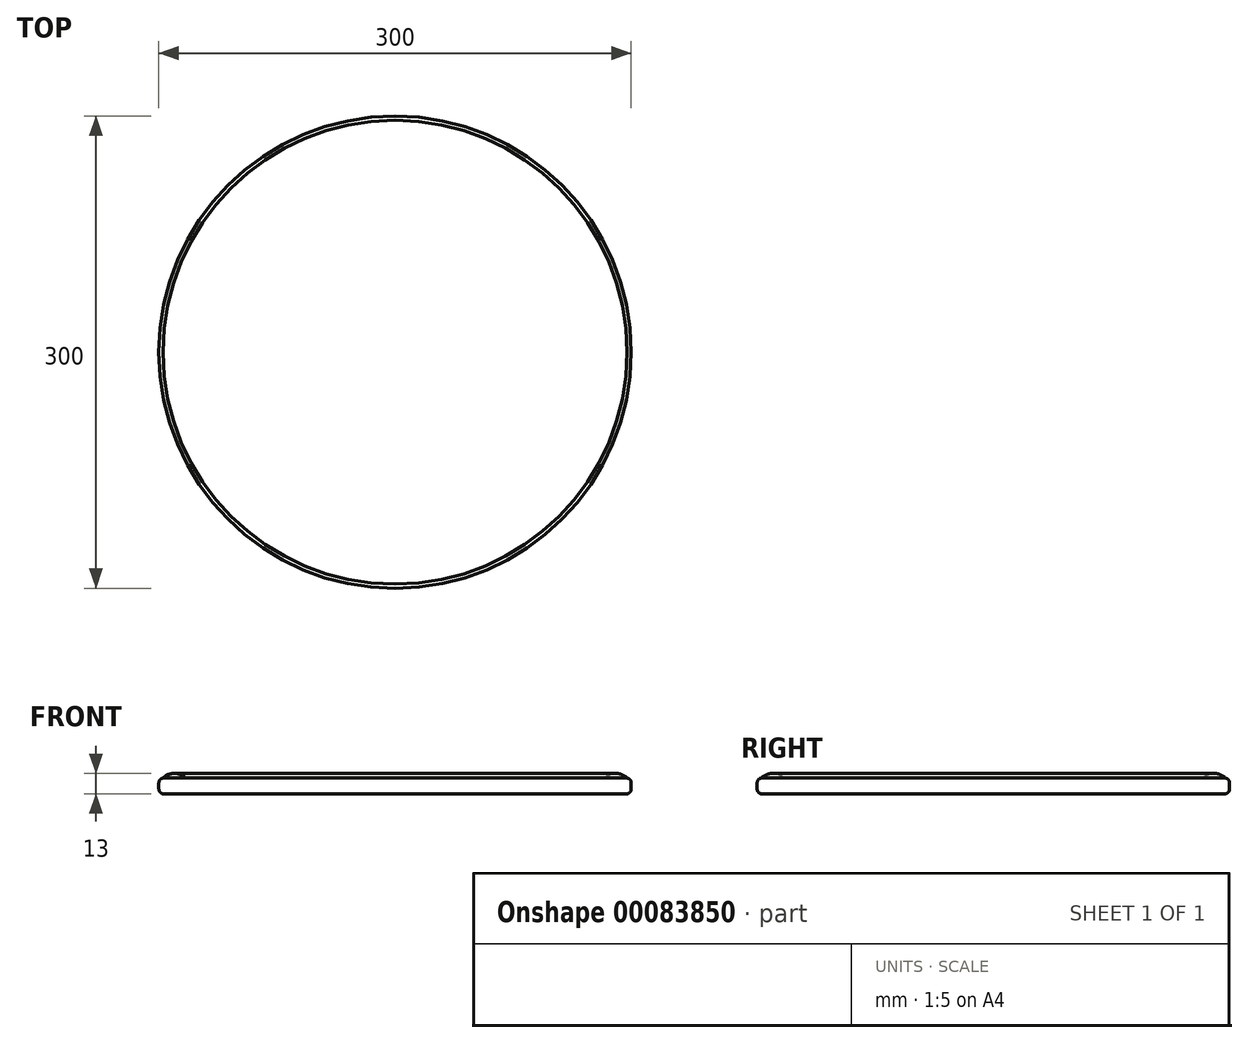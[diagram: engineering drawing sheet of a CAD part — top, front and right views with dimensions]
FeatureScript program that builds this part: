
annotation { "Feature Type Name" : "Feature", "Feature Type Description" : "" }
export const myFeature = defineFeature(function(context is Context, id is Id, definition is map)
    precondition{}
    {
        {
            var Q0;
            Q0=qCreatedBy(makeId("Top.planeOp"),FACE);
            var sketch = newSketch(context, id + "F0", { "sketchPlane" : qUnion([Q0])});
            skCircle(sketch, "E0", {"center": v(0, 0) * mm, "radius": 150 * mm});
            skSolve(sketch);
        }
        {
            var Q0;
            Q0=makeQuery(id+"F0.imprint","IMPRINT",FACE,{"disambiguationData":[TD([[makeQuery(id+"F0.imprint","IMPRINT",EDGE,{"derivedFrom":sQuery(id+"F0.wireOp",EDGE,"E0")}),1.0]])]});
            extrude(context, id + "F1", {"entities" : qUnion([Q0]), "depth" : 10 * mm});
        }
        {
            var Q0;
            Q0=qCreatedBy(makeId("Front.planeOp"),FACE);
            var sketch = newSketch(context, id + "F2", { "sketchPlane" : qUnion([Q0])});
            skArc(sketch, "E1", {"start": v(150, 5) * mm, "mid": v(140.2, 13) * mm, "end": v(130.4, 5) * mm});
            skLineSegment(sketch, "E2", {"start": v(130.4, 5) * mm, "end": v(150, 5) * mm});
            skLineSegment(sketch, "E3", {"start": v(0, 0) * mm, "end": v(0, 38.62) * mm, "construction": true});
            skSolve(sketch);
        }
        {
            var Q0;
            Q0=makeQuery(id+"F2.imprint","IMPRINT",FACE,{"disambiguationData":[TD([[makeQuery(id+"F2.imprint","IMPRINT",EDGE,{"derivedFrom":sQuery(id+"F2.wireOp",EDGE,"E1")}),1.0]])]});
            var Q1;
            Q1=sQuery(id+"F2.wireOp",EDGE,"E3");
            revolve(context, id + "F3", {"operationType" : NewBodyOperationType.ADD, "entities" : qUnion([Q0]), "axis" : qUnion([Q1]), "revolveType" : RevolveType.FULL});
        }
        {
            var Q0;
            Q0=makeQuery(id+"F1.opExtrude","SWEPT_FACE",FACE,{"disambiguationData":[OSD([sQuery(id+"F0.wireOp",EDGE,"E0")])]});
            var Q1;
            Q1=makeQuery(id+"F3.boolean.opBoolean","SPLIT",FACE,{"disambiguationData":[TD([makeQuery(id+"F3.opRevolve","SWEPT_FACE",FACE,{"disambiguationData":[OSD([sQuery(id+"F2.wireOp",EDGE,"E1")])]})])],"derivedFrom":makeQuery(id+"F1.opExtrude","CAP_FACE",FACE,{"disambiguationData":[OSD([sQuery(id+"F0.wireOp",EDGE,"E0")])],"isStart":false})});
            fillet(context, id + "F4", {"entities" : qUnion([Q0, Q1]), "radius" : 3 * mm, "tangentPropagation" : true, "allowEdgeOverflow" : false});
        }
    });
